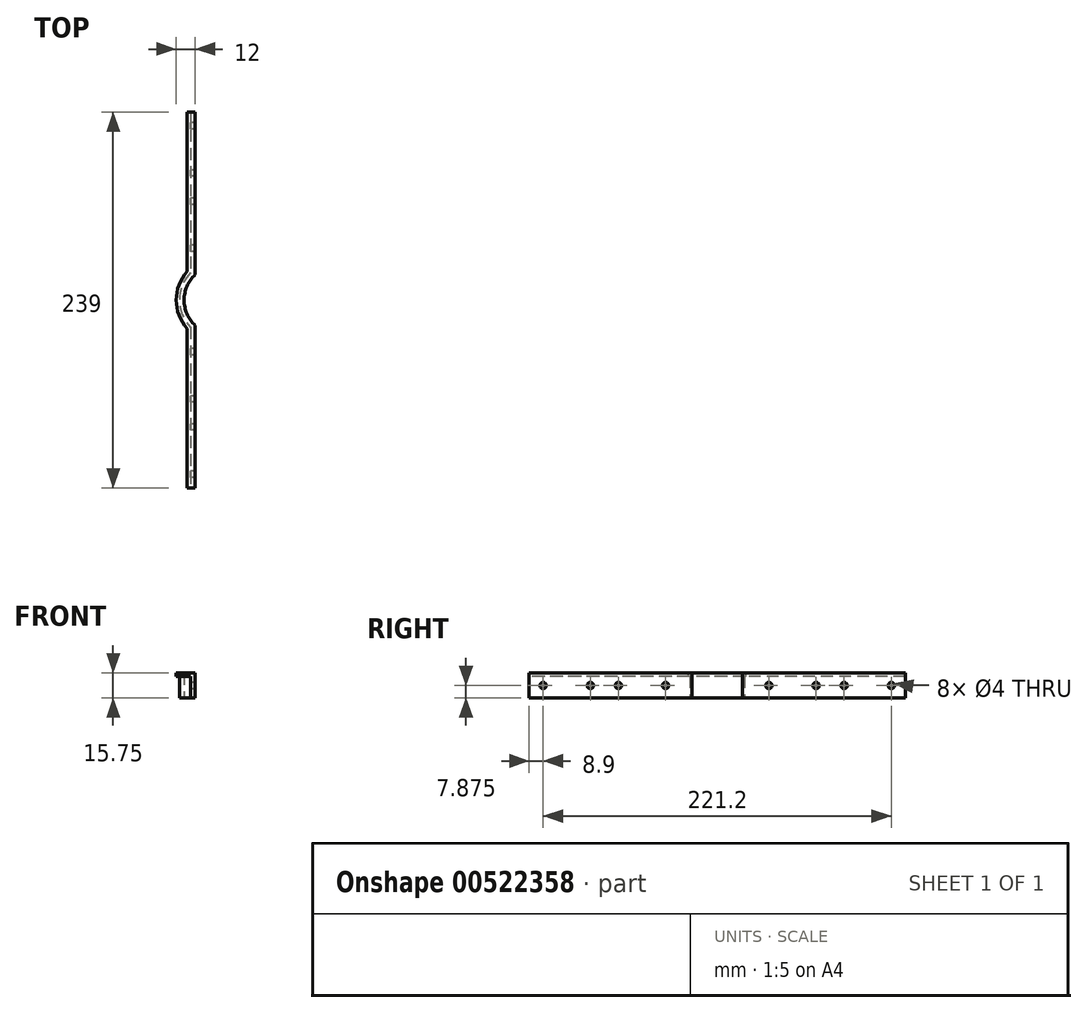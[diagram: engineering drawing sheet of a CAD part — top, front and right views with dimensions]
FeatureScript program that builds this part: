
annotation { "Feature Type Name" : "Feature", "Feature Type Description" : "" }
export const myFeature = defineFeature(function(context is Context, id is Id, definition is map)
    precondition{}
    {
        {
            var Q0;
            Q0=qCreatedBy(makeId("Top.planeOp"),FACE);
            var sketch = newSketch(context, id + "F0", { "sketchPlane" : qUnion([Q0])});
            skLineSegment(sketch, "E0.bottom", {"start": v(-18, 119.5) * mm, "end": v(-15, 119.5) * mm});
            skLineSegment(sketch, "E0.top", {"start": v(-18, -119.5) * mm, "end": v(-15, -119.5) * mm});
            skLineSegment(sketch, "E0.left", {"start": v(-18, 119.5) * mm, "end": v(-18, 17.35) * mm});
            skLineSegment(sketch, "E0.right", {"start": v(-15, 119.5) * mm, "end": v(-15, 16.1) * mm});
            skLineSegment(sketch, "E1", {"start": v(-16.5, 119.5) * mm, "end": v(-16.5, -119.5) * mm, "construction": true});
            skLineSegment(sketch, "E2", {"start": v(-18, 0) * mm, "end": v(-15, 0) * mm, "construction": true});
            skLineSegment(sketch, "E3", {"start": v(0, 0) * mm, "end": v(-16.5, 0) * mm, "construction": true});
            skLineSegment(sketch, "E4.trimOffspring", {"start": v(-15, -9.95) * mm, "end": v(-15, -119.5) * mm});
            skLineSegment(sketch, "E5.trimOffspring", {"start": v(-18, -11.87) * mm, "end": v(-18, -12.65) * mm});
            skArc(sketch, "E6", {"start": v(-15, 16.1) * mm, "mid": v(-22, 0) * mm, "end": v(-15, -16.1) * mm});
            skArc(sketch, "E7", {"start": v(-18, 17.35) * mm, "mid": v(-25, 0) * mm, "end": v(-18, -17.35) * mm});
            skLineSegment(sketch, "E8.trimOffspring", {"start": v(-18, -17.35) * mm, "end": v(-18, -119.5) * mm});
            skLineSegment(sketch, "E9.trimOffspring", {"start": v(-18, 12.65) * mm, "end": v(-18, 11.87) * mm});
            skSolve(sketch);
        }
        {
            var Q0;
            Q0=makeQuery(id+"F0.imprint","IMPRINT",FACE,{"disambiguationData":[TD([[makeQuery(id+"F0.imprint","IMPRINT",EDGE,{"derivedFrom":sQuery(id+"F0.wireOp",EDGE,"E0.bottom")}),-1.0]])]});
            extrude(context, id + "F1", {"entities" : qUnion([Q0]), "depth" : 15.75 * mm, "offsetDistance" : 25 * mm});
        }
        {
            var Q0;
            Q0=makeQuery(id+"F1.opExtrude","SWEPT_FACE",FACE,{"disambiguationData":[OSD([sQuery(id+"F0.wireOp",EDGE,"E0.left")])]});
            var sketch = newSketch(context, id + "F2", { "sketchPlane" : qUnion([Q0])});
            skLineSegment(sketch, "E10", {"start": v(-119.5, 7.88) * mm, "end": v(-119.5, 7.88) * mm});
            skLineSegment(sketch, "E11", {"start": v(-110.6, 15.75) * mm, "end": v(-110.6, 0) * mm, "construction": true});
            skLineSegment(sketch, "E12", {"start": v(-80.6, 15.75) * mm, "end": v(-80.6, 0) * mm, "construction": true});
            skLineSegment(sketch, "E13", {"start": v(-62.8, 15.75) * mm, "end": v(-62.8, 0) * mm, "construction": true});
            skPoint(sketch, "E13.endSnap0", {"position": v(-68.42, 0) * mm});
            skLineSegment(sketch, "E14", {"start": v(-32.8, 15.75) * mm, "end": v(-32.8, 0) * mm, "construction": true});
            skCircle(sketch, "E15", {"center": v(-110.6, 7.88) * mm, "radius": 2 * mm});
            skCircle(sketch, "E16", {"center": v(-80.6, 7.88) * mm, "radius": 2 * mm});
            skCircle(sketch, "E17", {"center": v(-62.8, 7.88) * mm, "radius": 2 * mm});
            skCircle(sketch, "E18", {"center": v(-32.8, 7.88) * mm, "radius": 2 * mm});
            skSolve(sketch);
        }
        {
            var Q0;
            Q0=makeQuery(id+"F1.opExtrude","SWEPT_FACE",FACE,{"disambiguationData":[OSD([sQuery(id+"F0.wireOp",EDGE,"E8.trimOffspring")])]});
            var sketch = newSketch(context, id + "F3", { "sketchPlane" : qUnion([Q0])});
            skLineSegment(sketch, "E19", {"start": v(110.6, 15.75) * mm, "end": v(110.6, 0) * mm, "construction": true});
            skLineSegment(sketch, "E20", {"start": v(80.6, 15.75) * mm, "end": v(80.6, 0) * mm, "construction": true});
            skLineSegment(sketch, "E21", {"start": v(62.8, 15.75) * mm, "end": v(62.8, 0) * mm, "construction": true});
            skLineSegment(sketch, "E22", {"start": v(32.8, 15.75) * mm, "end": v(32.8, 0) * mm, "construction": true});
            skCircle(sketch, "E23", {"center": v(110.6, 7.88) * mm, "radius": 2 * mm});
            skCircle(sketch, "E24", {"center": v(80.6, 7.88) * mm, "radius": 2 * mm});
            skCircle(sketch, "E25", {"center": v(62.8, 7.88) * mm, "radius": 2 * mm});
            skCircle(sketch, "E26", {"center": v(32.8, 7.88) * mm, "radius": 2 * mm});
            skSolve(sketch);
        }
        {
            var Q0;
            Q0=makeQuery(id+"F2.imprint","IMPRINT",FACE,{"disambiguationData":[TD([[makeQuery(id+"F2.imprint","IMPRINT",EDGE,{"derivedFrom":sQuery(id+"F2.wireOp",EDGE,"E15")}),1.0]])]});
            var Q1;
            Q1=makeQuery(id+"F2.imprint","IMPRINT",FACE,{"disambiguationData":[TD([[makeQuery(id+"F2.imprint","IMPRINT",EDGE,{"derivedFrom":sQuery(id+"F2.wireOp",EDGE,"E16")}),1.0]])]});
            var Q2;
            Q2=makeQuery(id+"F2.imprint","IMPRINT",FACE,{"disambiguationData":[TD([[makeQuery(id+"F2.imprint","IMPRINT",EDGE,{"derivedFrom":sQuery(id+"F2.wireOp",EDGE,"E17")}),1.0]])]});
            var Q3;
            Q3=makeQuery(id+"F2.imprint","IMPRINT",FACE,{"disambiguationData":[TD([[makeQuery(id+"F2.imprint","IMPRINT",EDGE,{"derivedFrom":sQuery(id+"F2.wireOp",EDGE,"E18")}),1.0]])]});
            var Q4;
            Q4=makeQuery(id+"F3.imprint","IMPRINT",FACE,{"disambiguationData":[TD([[makeQuery(id+"F3.imprint","IMPRINT",EDGE,{"derivedFrom":sQuery(id+"F3.wireOp",EDGE,"HgL4I013-YLYd-WOwv-trkV-jnHJ1rwzCFBG")}),1.0]])]});
            var Q5;
            Q5=makeQuery(id+"F3.imprint","IMPRINT",FACE,{"disambiguationData":[TD([[makeQuery(id+"F3.imprint","IMPRINT",EDGE,{"derivedFrom":sQuery(id+"F3.wireOp",EDGE,"gCeuhB68-pwRE-myV2-M7Lv-yfLO9Kip18Ak")}),1.0]])]});
            var Q6;
            Q6=makeQuery(id+"F3.imprint","IMPRINT",FACE,{"disambiguationData":[TD([[makeQuery(id+"F3.imprint","IMPRINT",EDGE,{"derivedFrom":sQuery(id+"F3.wireOp",EDGE,"BPU1QgK7-vlWH-zAnu-a8sJ-TJr8QqGD27dm")}),1.0]])]});
            var Q7;
            Q7=makeQuery(id+"F3.imprint","IMPRINT",FACE,{"disambiguationData":[TD([[makeQuery(id+"F3.imprint","IMPRINT",EDGE,{"derivedFrom":sQuery(id+"F3.wireOp",EDGE,"ibDlLswx-uESJ-GVcY-kckd-uM0a5gnpvbbg")}),1.0]])]});
            extrude(context, id + "F4", {"entities" : qUnion([Q0, Q1, Q2, Q3, Q4, Q5, Q6, Q7]), "operationType" : NewBodyOperationType.REMOVE, "endBound" : BoundingType.THROUGH_ALL, "oppositeDirection" : true, "depth" : 25 * mm, "offsetDistance" : 25 * mm});
        }
        {
            var Q0;
            Q0=makeQuery(id+"F3.imprint","IMPRINT",FACE,{"disambiguationData":[TD([[makeQuery(id+"F3.imprint","IMPRINT",EDGE,{"derivedFrom":sQuery(id+"F3.wireOp",EDGE,"E26")}),1.0]])]});
            var Q1;
            Q1=makeQuery(id+"F3.imprint","IMPRINT",FACE,{"disambiguationData":[TD([[makeQuery(id+"F3.imprint","IMPRINT",EDGE,{"derivedFrom":sQuery(id+"F3.wireOp",EDGE,"E25")}),1.0]])]});
            var Q2;
            Q2=makeQuery(id+"F3.imprint","IMPRINT",FACE,{"disambiguationData":[TD([[makeQuery(id+"F3.imprint","IMPRINT",EDGE,{"derivedFrom":sQuery(id+"F3.wireOp",EDGE,"E24")}),1.0]])]});
            var Q3;
            Q3=makeQuery(id+"F3.imprint","IMPRINT",FACE,{"disambiguationData":[TD([[makeQuery(id+"F3.imprint","IMPRINT",EDGE,{"derivedFrom":sQuery(id+"F3.wireOp",EDGE,"E23")}),1.0]])]});
            extrude(context, id + "F5", {"entities" : qUnion([Q0, Q1, Q2, Q3]), "operationType" : NewBodyOperationType.REMOVE, "endBound" : BoundingType.THROUGH_ALL, "oppositeDirection" : true, "depth" : 25 * mm, "offsetDistance" : 25 * mm});
        }
        {
            var Q0;
            Q0=makeQuery(id+"F1.opExtrude","CAP_FACE",FACE,{"disambiguationData":[OSD([sQuery(id+"F0.wireOp",EDGE,"E0.bottom"),sQuery(id+"F0.wireOp",EDGE,"E0.top"),sQuery(id+"F0.wireOp",EDGE,"E0.left"),sQuery(id+"F0.wireOp",EDGE,"E0.right"),sQuery(id+"F0.wireOp",EDGE,"E4.trimOffspring"),sQuery(id+"F0.wireOp",EDGE,"E6"),sQuery(id+"F0.wireOp",EDGE,"E7"),sQuery(id+"F0.wireOp",EDGE,"E8.trimOffspring")])],"isStart":false});
            var sketch = newSketch(context, id + "F6", { "sketchPlane" : qUnion([Q0])});
            skLineSegment(sketch, "E27.0", {"start": v(-20, -18.14) * mm, "end": v(-20, -119.5) * mm});
            skArc(sketch, "E27.1", {"start": v(-20, 18.14) * mm, "mid": v(-27, 0) * mm, "end": v(-20, -18.14) * mm});
            skLineSegment(sketch, "E27.2", {"start": v(-20, 119.5) * mm, "end": v(-20, 18.14) * mm});
            skLineSegment(sketch, "E28", {"start": v(-20, 119.5) * mm, "end": v(-18, 119.5) * mm});
            skLineSegment(sketch, "E29", {"start": v(-20, -119.5) * mm, "end": v(-18, -119.5) * mm});
            skSolve(sketch);
        }
        {
            var Q0;
            Q0=makeQuery(id+"F6.imprint","IMPRINT",FACE,{"disambiguationData":[TD([[makeQuery(id+"F6.imprint","IMPRINT",EDGE,{"derivedFrom":sQuery(id+"F6.wireOp",EDGE,"E27.0")}),1.0]])]});
            extrude(context, id + "F7", {"entities" : qUnion([Q0]), "operationType" : NewBodyOperationType.ADD, "oppositeDirection" : true, "depth" : 2 * mm, "offsetDistance" : 25 * mm});
        }
    });
